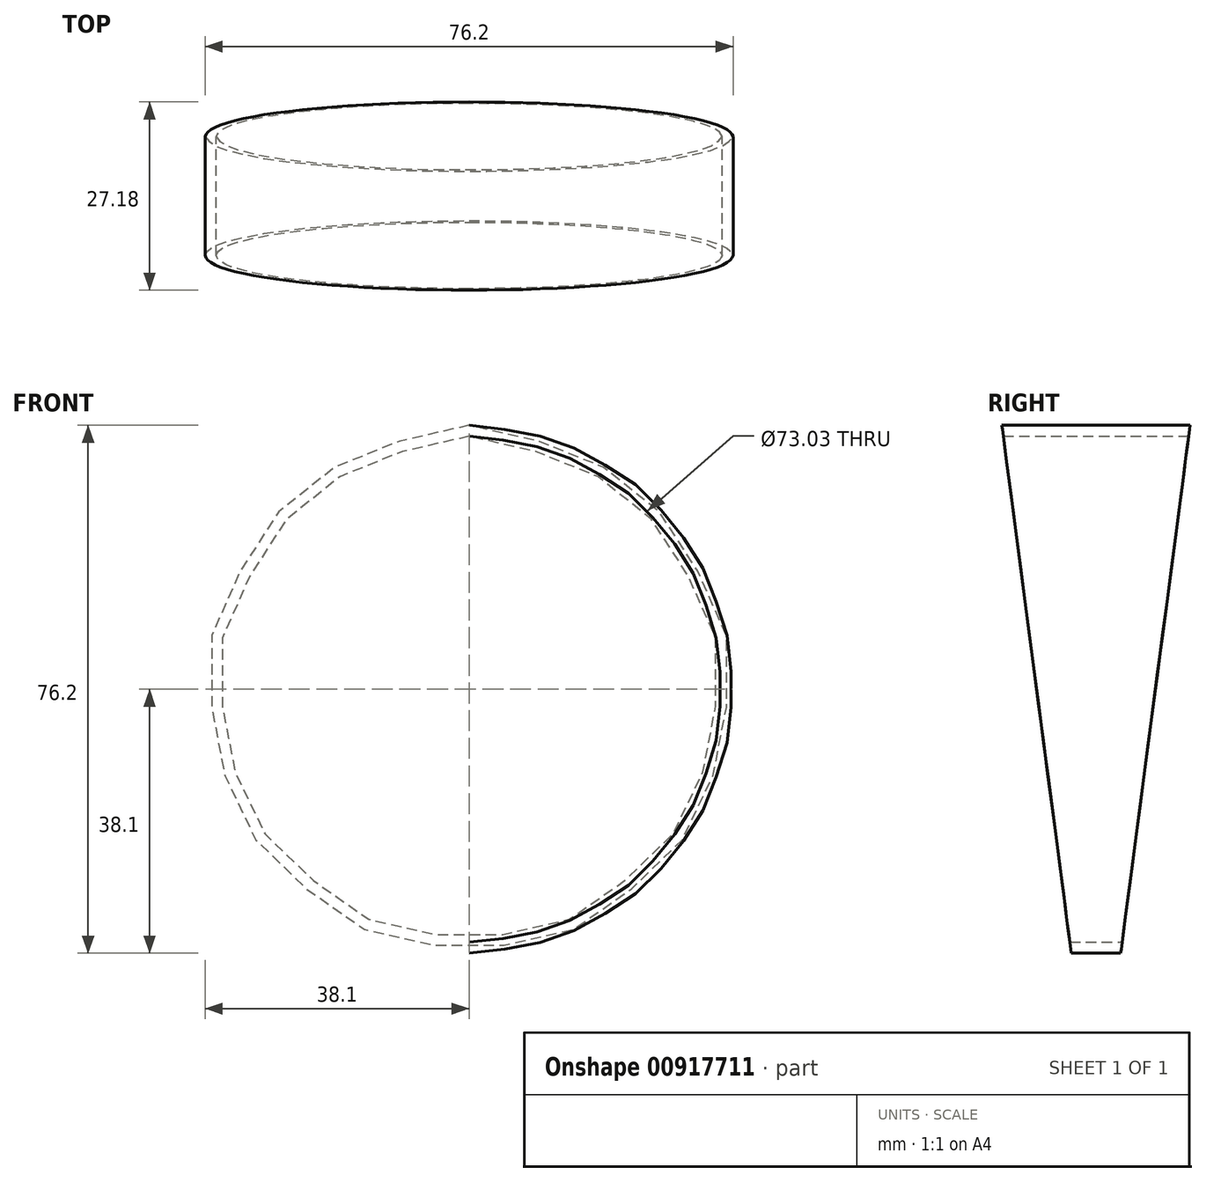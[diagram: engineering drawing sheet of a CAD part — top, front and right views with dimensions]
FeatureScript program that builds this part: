
annotation { "Feature Type Name" : "Feature", "Feature Type Description" : "" }
export const myFeature = defineFeature(function(context is Context, id is Id, definition is map)
    precondition{}
    {
        {
            var Q0;
            Q0=qCreatedBy(makeId("Front.planeOp"),FACE);
            var sketch = newSketch(context, id + "F0", { "sketchPlane" : qUnion([Q0])});
            skCircle(sketch, "E0", {"center": v(0, 38.1) * mm, "radius": 38.1 * mm});
            skCircle(sketch, "E1", {"center": v(0, 38.1) * mm, "radius": 36.51 * mm});
            skPoint(sketch, "E2", {"position": v(0, 0) * mm});
            skSolve(sketch);
        }
        {
            var Q0;
            Q0 = qSketchRegion(id + "F0", true);
            extrude(context, id + "F1", {"entities" : qUnion([Q0]), "depth" : 27.18 * mm, "offsetDistance" : 25.4 * mm, "symmetric" : true});
        }
        {
            var Q0;
            Q0=qCreatedBy(makeId("Right.planeOp"),FACE);
            var sketch = newSketch(context, id + "F2", { "sketchPlane" : qUnion([Q0])});
            skLineSegment(sketch, "E3", {"start": v(-3.56, 0) * mm, "end": v(3.56, 0) * mm});
            skLineSegment(sketch, "E4", {"start": v(13.59, 76.2) * mm, "end": v(13.59, -15.07) * mm});
            skLineSegment(sketch, "E5", {"start": v(13.59, -15.07) * mm, "end": v(-13.59, -15.07) * mm});
            skLineSegment(sketch, "E6", {"start": v(-13.59, -15.07) * mm, "end": v(-13.59, 76.2) * mm});
            skPoint(sketch, "E7", {"position": v(0, 0) * mm});
            skPoint(sketch, "E8", {"position": v(0, -15.07) * mm});
            skLineSegment(sketch, "E9", {"start": v(-13.59, 76.2) * mm, "end": v(-3.56, 0) * mm});
            skLineSegment(sketch, "E10", {"start": v(13.59, 76.2) * mm, "end": v(3.56, 0) * mm});
            skSolve(sketch);
        }
        {
            var Q0;
            Q0 = qSketchRegion(id + "F2", true);
            extrude(context, id + "F3", {"entities" : qUnion([Q0]), "operationType" : NewBodyOperationType.REMOVE, "oppositeDirection" : true, "depth" : 127 * mm, "offsetDistance" : 25.4 * mm, "symmetric" : true});
        }
    });
